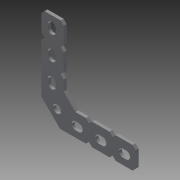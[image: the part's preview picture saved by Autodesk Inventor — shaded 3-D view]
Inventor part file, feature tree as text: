
AUTODESK INVENTOR PART (.ipt)
format: ipt  version: 2015 (Build 190159000, 159)  size: 165,888 bytes
history: native  units: in
note: dims shown in document units (in); Inventor stores cm internally (conversion verified against a paired STEP export)
features: other x1, chamfer x1, imported_body x1
ambient origin geometry x8: Origin, YZ Plane, XZ Plane, XY Plane, X Axis, Y Axis, Z Axis, Center Point
bodies: Body1 (feature_tree)
feature tree (3):
  other  "Right-Angle Bar Gusset"
  chamfer  "Chamfer1"  [1 undecoded]
  imported_body  "Base1"
note: 1 required parameter value undecoded (feature->parameter linkage not recoverable at this tier; creation-order binding heuristic only, values carry confidence <= 0.55)
